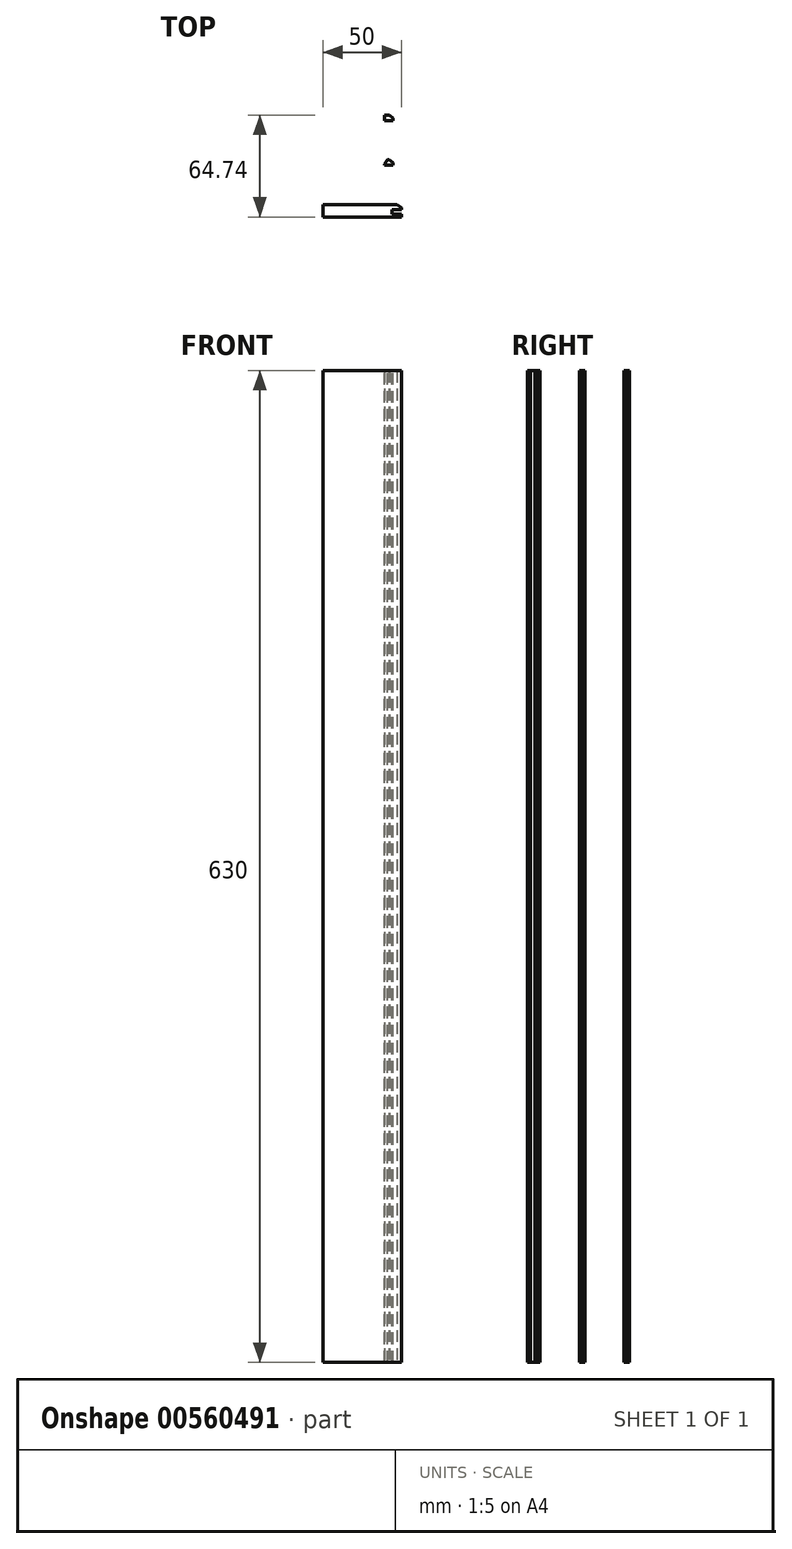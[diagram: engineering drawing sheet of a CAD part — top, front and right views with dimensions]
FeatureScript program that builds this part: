
annotation { "Feature Type Name" : "Feature", "Feature Type Description" : "" }
export const myFeature = defineFeature(function(context is Context, id is Id, definition is map)
    precondition{}
    {
        {
            var Q0;
            Q0=qCreatedBy(makeId("Top.planeOp"),FACE);
            var sketch = newSketch(context, id + "F0", { "sketchPlane" : qUnion([Q0])});
            skLineSegment(sketch, "E0.bottom", {"start": v(45.75, 4) * mm, "end": v(-45.75, 4) * mm});
            skLineSegment(sketch, "E0.top", {"start": v(45.75, -4) * mm, "end": v(-45.75, -4) * mm});
            skLineSegment(sketch, "E0.left", {"start": v(45.75, 4) * mm, "end": v(45.75, -4) * mm});
            skLineSegment(sketch, "E0.right", {"start": v(-45.75, 4) * mm, "end": v(-45.75, -4) * mm});
            skPoint(sketch, "E0.middle", {"position": v(0, 0) * mm});
            skLineSegment(sketch, "E1.bottom", {"start": v(45.75, -2) * mm, "end": v(39.75, -2) * mm});
            skLineSegment(sketch, "E1.top", {"start": v(45.75, 0.6) * mm, "end": v(39.75, 0.6) * mm});
            skLineSegment(sketch, "E1.left", {"start": v(45.75, -2) * mm, "end": v(45.75, 0.6) * mm});
            skLineSegment(sketch, "E1.right", {"start": v(39.75, -2) * mm, "end": v(39.75, 0.6) * mm});
            skPoint(sketch, "E1.middle", {"position": v(42.75, -0.7) * mm});
            skLineSegment(sketch, "E2.bottom", {"start": v(-45.75, -4) * mm, "end": v(-40.25, -4) * mm});
            skLineSegment(sketch, "E2.top", {"start": v(-45.75, -2) * mm, "end": v(-40.25, -2) * mm});
            skLineSegment(sketch, "E2.left", {"start": v(-45.75, -4) * mm, "end": v(-45.75, -2) * mm});
            skLineSegment(sketch, "E2.right", {"start": v(-40.25, -4) * mm, "end": v(-40.25, -2) * mm});
            skLineSegment(sketch, "E3.bottom", {"start": v(-45.75, 0.5) * mm, "end": v(-40.25, 0.5) * mm});
            skLineSegment(sketch, "E3.top", {"start": v(-45.75, 4) * mm, "end": v(-40.25, 4) * mm});
            skLineSegment(sketch, "E3.left", {"start": v(-45.75, 0.5) * mm, "end": v(-45.75, 4) * mm});
            skLineSegment(sketch, "E3.right", {"start": v(-40.25, 0.5) * mm, "end": v(-40.25, 4) * mm});
            skLineSegment(sketch, "E4.bottom", {"start": v(-34.82, -24.44) * mm, "end": v(-84.82, -24.44) * mm});
            skLineSegment(sketch, "E4.top", {"start": v(-34.82, -32.44) * mm, "end": v(-84.82, -32.44) * mm});
            skLineSegment(sketch, "E4.left", {"start": v(-34.82, -24.44) * mm, "end": v(-34.82, -32.44) * mm});
            skLineSegment(sketch, "E4.right", {"start": v(-84.82, -24.44) * mm, "end": v(-84.82, -32.44) * mm});
            skPoint(sketch, "E4.middle", {"position": v(-59.82, -28.44) * mm});
            skLineSegment(sketch, "E5.bottom", {"start": v(-34.82, -30.44) * mm, "end": v(-40.82, -30.44) * mm});
            skLineSegment(sketch, "E5.top", {"start": v(-34.82, -27.84) * mm, "end": v(-40.82, -27.84) * mm});
            skLineSegment(sketch, "E5.left", {"start": v(-34.82, -30.44) * mm, "end": v(-34.82, -27.84) * mm});
            skLineSegment(sketch, "E5.right", {"start": v(-40.82, -30.44) * mm, "end": v(-40.82, -27.84) * mm});
            skPoint(sketch, "E5.middle", {"position": v(-37.82, -29.14) * mm});
            skLineSegment(sketch, "E6.bottom", {"start": v(-84.82, -32.44) * mm, "end": v(-40.32, -32.44) * mm});
            skLineSegment(sketch, "E6.left", {"start": v(-84.82, -32.44) * mm, "end": v(-84.82, -30.44) * mm});
            skLineSegment(sketch, "E7.top", {"start": v(-84.82, -24.44) * mm, "end": v(-79.32, -24.44) * mm});
            skPoint(sketch, "E8.middle", {"position": v(-0.95, -28.36) * mm});
            skLineSegment(sketch, "E9.bottom", {"start": v(-45.82, -32.44) * mm, "end": v(-40.32, -32.44) * mm});
            skLineSegment(sketch, "E9.left", {"start": v(-45.82, -32.44) * mm, "end": v(-45.82, -30.44) * mm});
            skLineSegment(sketch, "E10.bottom", {"start": v(9.77, 32.3) * mm, "end": v(-45.73, 32.3) * mm});
            skLineSegment(sketch, "E10.top", {"start": v(9.77, 24.3) * mm, "end": v(-45.73, 24.3) * mm});
            skLineSegment(sketch, "E10.left", {"start": v(9.77, 32.3) * mm, "end": v(9.77, 24.3) * mm});
            skLineSegment(sketch, "E10.right", {"start": v(-45.73, 32.3) * mm, "end": v(-45.73, 24.3) * mm});
            skPoint(sketch, "E10.middle", {"position": v(-17.98, 28.3) * mm});
            skLineSegment(sketch, "E11.left", {"start": v(9.77, 26.3) * mm, "end": v(9.77, 28.9) * mm});
            skLineSegment(sketch, "E12.bottom", {"start": v(-45.73, 24.3) * mm, "end": v(-40.23, 24.3) * mm});
            skLineSegment(sketch, "E12.top", {"start": v(-45.73, 26.3) * mm, "end": v(-40.23, 26.3) * mm});
            skLineSegment(sketch, "E12.left", {"start": v(-45.73, 24.3) * mm, "end": v(-45.73, 26.3) * mm});
            skLineSegment(sketch, "E12.right", {"start": v(-40.23, 24.3) * mm, "end": v(-40.23, 26.3) * mm});
            skLineSegment(sketch, "E13.bottom", {"start": v(-45.73, 28.8) * mm, "end": v(-40.23, 28.8) * mm});
            skLineSegment(sketch, "E13.top", {"start": v(-45.73, 32.3) * mm, "end": v(-40.23, 32.3) * mm});
            skLineSegment(sketch, "E13.left", {"start": v(-45.73, 28.8) * mm, "end": v(-45.73, 32.3) * mm});
            skLineSegment(sketch, "E13.right", {"start": v(-40.23, 28.8) * mm, "end": v(-40.23, 32.3) * mm});
            skSolve(sketch);
        }
        {
            var Q0;
            {var subQ2=sQuery(id+"F0.wireOp",EDGE,"E0.bottom");Q0=makeQuery(id+"F0.imprint","IMPRINT",FACE,{"disambiguationData":[TD([[makeQuery(id+"F0.imprint","IMPRINT",EDGE,{"derivedFrom":subQ2}),1.0]])]});}
            extrude(context, id + "F1", {"entities" : qUnion([Q0]), "oppositeDirection" : true, "depth" : 630 * mm, "offsetDistance" : 25 * mm});
        }
        {
            var Q0;
            Q0=makeQuery(id+"F1.opExtrude","SWEPT_EDGE",EDGE,{"disambiguationData":[OSD([sQuery(id+"F0.wireOp",EDGE,"E0.bottom"),sQuery(id+"F0.wireOp",EDGE,"E3.top"),sQuery(id+"F0.wireOp",EDGE,"E3.right")])]});
            chamfer(context, id + "F2", {"entities" : qUnion([Q0]), "chamferType" : ChamferType.OFFSET_ANGLE, "width" : 2 * mm, "oppositeDirection" : false, "angle" : 50 * degree, "tangentPropagation" : true});
        }
        {
            var Q0;
            Q0=makeQuery(id+"F1.opExtrude","SWEPT_EDGE",EDGE,{"disambiguationData":[OSD([sQuery(id+"F0.wireOp",EDGE,"E0.bottom"),sQuery(id+"F0.wireOp",EDGE,"E0.left")])]});
            chamfer(context, id + "F3", {"entities" : qUnion([Q0]), "chamferType" : ChamferType.OFFSET_ANGLE, "width" : 2 * mm, "oppositeDirection" : false, "angle" : 55 * degree, "tangentPropagation" : true});
        }
        {
            var Q0;
            {var subQ3=sQuery(id+"F0.wireOp",EDGE,"E10.bottom");Q0=makeQuery(id+"F0.imprint","IMPRINT",FACE,{"disambiguationData":[TD([[makeQuery(id+"F0.imprint","IMPRINT",EDGE,{"derivedFrom":subQ3}),1.0]])]});}
            extrude(context, id + "F4", {"entities" : qUnion([Q0]), "oppositeDirection" : true, "depth" : 630 * mm, "offsetDistance" : 25 * mm});
        }
        {
            var Q0;
            {var subQ2=sQuery(id+"F0.wireOp",EDGE,"E4.bottom");Q0=makeQuery(id+"F0.imprint","IMPRINT",FACE,{"disambiguationData":[TD([[makeQuery(id+"F0.imprint","IMPRINT",EDGE,{"derivedFrom":subQ2}),1.0]])]});}
            extrude(context, id + "F5", {"entities" : qUnion([Q0]), "oppositeDirection" : true, "depth" : 630 * mm, "offsetDistance" : 25 * mm});
        }
        {
            var Q0;
            Q0=makeQuery(id+"F4.opExtrude","SWEPT_EDGE",EDGE,{"disambiguationData":[OSD([sQuery(id+"F0.wireOp",EDGE,"E10.bottom"),sQuery(id+"F0.wireOp",EDGE,"E13.top"),sQuery(id+"F0.wireOp",EDGE,"E13.right")])]});
            chamfer(context, id + "F6", {"entities" : qUnion([Q0]), "chamferType" : ChamferType.OFFSET_ANGLE, "width" : 2 * mm, "oppositeDirection" : false, "angle" : 50 * degree, "tangentPropagation" : true});
        }
        {
            var Q0;
            Q0=makeQuery(id+"F5.opExtrude","SWEPT_EDGE",EDGE,{"disambiguationData":[OSD([sQuery(id+"F0.wireOp",EDGE,"E4.bottom"),sQuery(id+"F0.wireOp",EDGE,"E4.left")])]});
            chamfer(context, id + "F7", {"entities" : qUnion([Q0]), "chamferType" : ChamferType.OFFSET_ANGLE, "width" : 2 * mm, "oppositeDirection" : false, "angle" : 55 * degree, "tangentPropagation" : true});
        }
    });
